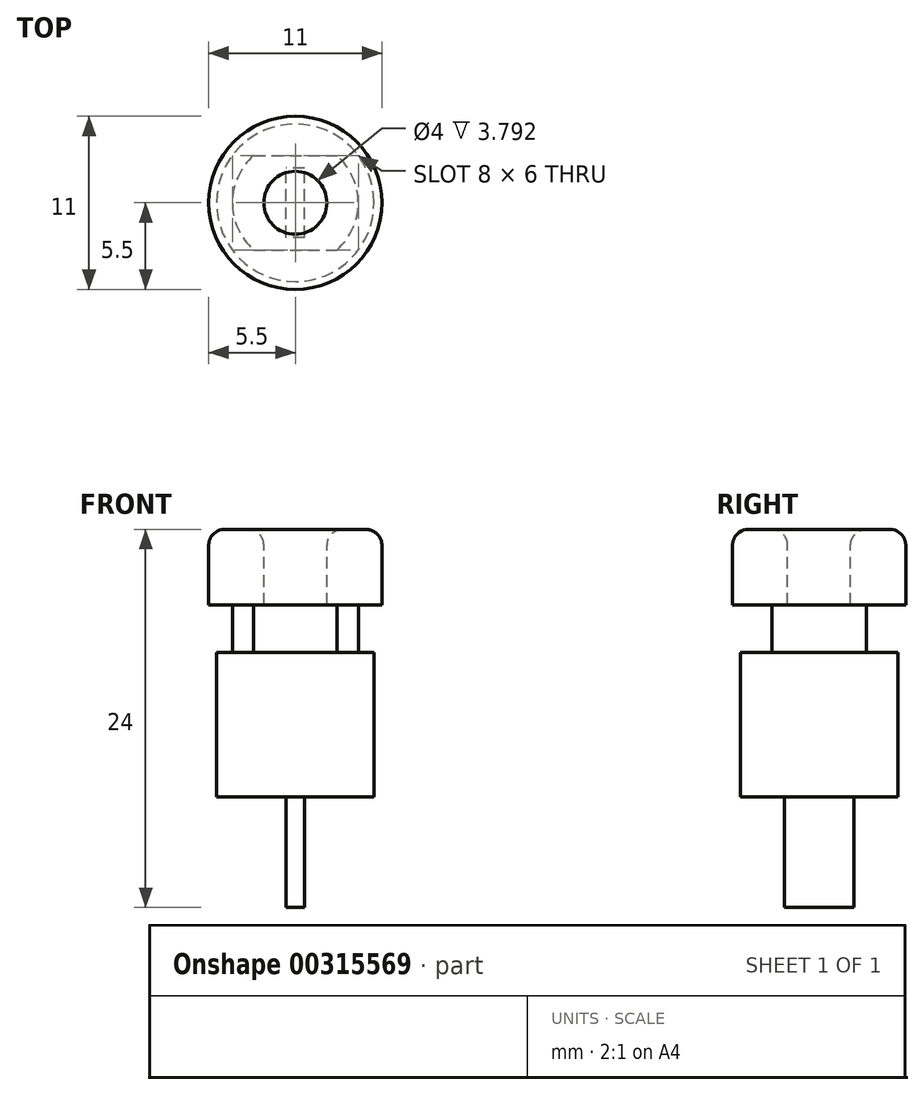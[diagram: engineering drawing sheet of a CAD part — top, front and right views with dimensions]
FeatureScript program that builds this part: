
annotation { "Feature Type Name" : "Feature", "Feature Type Description" : "" }
export const myFeature = defineFeature(function(context is Context, id is Id, definition is map)
    precondition{}
    {
        {
            var Q0;
            Q0=qCreatedBy(makeId("Front.planeOp"),FACE);
            var sketch = newSketch(context, id + "F0", { "sketchPlane" : qUnion([Q0])});
            skLineSegment(sketch, "E0", {"start": v(2, 4.8) * mm, "end": v(5.5, 4.8) * mm});
            skLineSegment(sketch, "E1", {"start": v(5.5, 4.8) * mm, "end": v(5.5, 0) * mm});
            skLineSegment(sketch, "E2", {"start": v(5.5, 0) * mm, "end": v(4, 0) * mm});
            skLineSegment(sketch, "E3", {"start": v(4, 0) * mm, "end": v(4, -3) * mm});
            skLineSegment(sketch, "E4", {"start": v(4, -3) * mm, "end": v(5, -3) * mm});
            skLineSegment(sketch, "E5", {"start": v(5, -3) * mm, "end": v(5, -12.2) * mm});
            skLineSegment(sketch, "E6", {"start": v(5, -12.2) * mm, "end": v(0, -12.2) * mm});
            skLineSegment(sketch, "E7", {"start": v(0, -12.2) * mm, "end": v(0, 0) * mm});
            skLineSegment(sketch, "E8", {"start": v(0, 0) * mm, "end": v(2, 0) * mm});
            skLineSegment(sketch, "E9", {"start": v(2, 0) * mm, "end": v(2, 4.8) * mm});
            skPoint(sketch, "E10.orphan", {"position": v(0, 4.8) * mm});
            skLineSegment(sketch, "E11", {"start": v(0, 38.98) * mm, "end": v(0, -12.2) * mm, "construction": true});
            skSolve(sketch);
        }
        {
            var Q0;
            Q0 = qSketchRegion(id + "F0", true);
            var Q1;
            Q1=sQuery(id+"F0.wireOp",EDGE,"E11");
            revolve(context, id + "F1", {"entities" : qUnion([Q0]), "axis" : qUnion([Q1]), "revolveType" : RevolveType.FULL});
        }
        {
            var Q0;
            Q0=makeQuery(id+"F1.opRevolve","SWEPT_EDGE",EDGE,{"disambiguationData":[OSD([sQuery(id+"F0.wireOp",EDGE,"E0"),sQuery(id+"F0.wireOp",EDGE,"E1")])]});
            var Q1;
            Q1=makeQuery(id+"F1.opRevolve","SWEPT_EDGE",EDGE,{"disambiguationData":[OSD([sQuery(id+"F0.wireOp",EDGE,"E0"),sQuery(id+"F0.wireOp",EDGE,"E9")])]});
            fillet(context, id + "F2", {"entities" : qUnion([Q0, Q1]), "radius" : 1 * mm, "tangentPropagation" : true, "allowEdgeOverflow" : false});
        }
        {
            var Q0;
            Q0=makeQuery(id+"F1.opRevolve","SWEPT_FACE",FACE,{"disambiguationData":[OSD([sQuery(id+"F0.wireOp",EDGE,"E6")])]});
            var sketch = newSketch(context, id + "F3", { "sketchPlane" : qUnion([Q0])});
            skLineSegment(sketch, "E12.bottom", {"start": v(0.6, 2.2) * mm, "end": v(-0.6, 2.2) * mm});
            skLineSegment(sketch, "E12.top", {"start": v(0.6, -2.2) * mm, "end": v(-0.6, -2.2) * mm});
            skLineSegment(sketch, "E12.left", {"start": v(0.6, 2.2) * mm, "end": v(0.6, -2.2) * mm});
            skLineSegment(sketch, "E12.right", {"start": v(-0.6, 2.2) * mm, "end": v(-0.6, -2.2) * mm});
            skPoint(sketch, "E12.middle", {"position": v(0, 0) * mm});
            skSolve(sketch);
        }
        {
            var Q0;
            Q0 = qSketchRegion(id + "F3", true);
            extrude(context, id + "F4", {"entities" : qUnion([Q0]), "operationType" : NewBodyOperationType.ADD, "depth" : 7 * mm});
        }
        {
            var Q0;
            Q0=qCreatedBy(makeId("Right.planeOp"),FACE);
            var sketch = newSketch(context, id + "F5", { "sketchPlane" : qUnion([Q0])});
            skLineSegment(sketch, "E13.bottom", {"start": v(3, 0) * mm, "end": v(4.68, 0) * mm});
            skLineSegment(sketch, "E13.top", {"start": v(3, -3) * mm, "end": v(4.68, -3) * mm});
            skLineSegment(sketch, "E13.left", {"start": v(3, 0) * mm, "end": v(3, -3) * mm});
            skLineSegment(sketch, "E13.right", {"start": v(4.68, 0) * mm, "end": v(4.68, -3) * mm});
            skLineSegment(sketch, "E14.bottom", {"start": v(-3, 0) * mm, "end": v(-4.4, 0) * mm});
            skLineSegment(sketch, "E14.top", {"start": v(-3, -3) * mm, "end": v(-4.4, -3) * mm});
            skLineSegment(sketch, "E14.left", {"start": v(-3, 0) * mm, "end": v(-3, -3) * mm});
            skLineSegment(sketch, "E14.right", {"start": v(-4.4, 0) * mm, "end": v(-4.4, -3) * mm});
            skLineSegment(sketch, "E15", {"start": v(0, 0) * mm, "end": v(0, -2.88) * mm, "construction": true});
            skSolve(sketch);
        }
        {
            var Q0;
            Q0 = qSketchRegion(id + "F5", true);
            extrude(context, id + "F6", {"entities" : qUnion([Q0]), "operationType" : NewBodyOperationType.REMOVE, "oppositeDirection" : true, "depth" : 25 * mm, "symmetric" : true});
        }
    });
